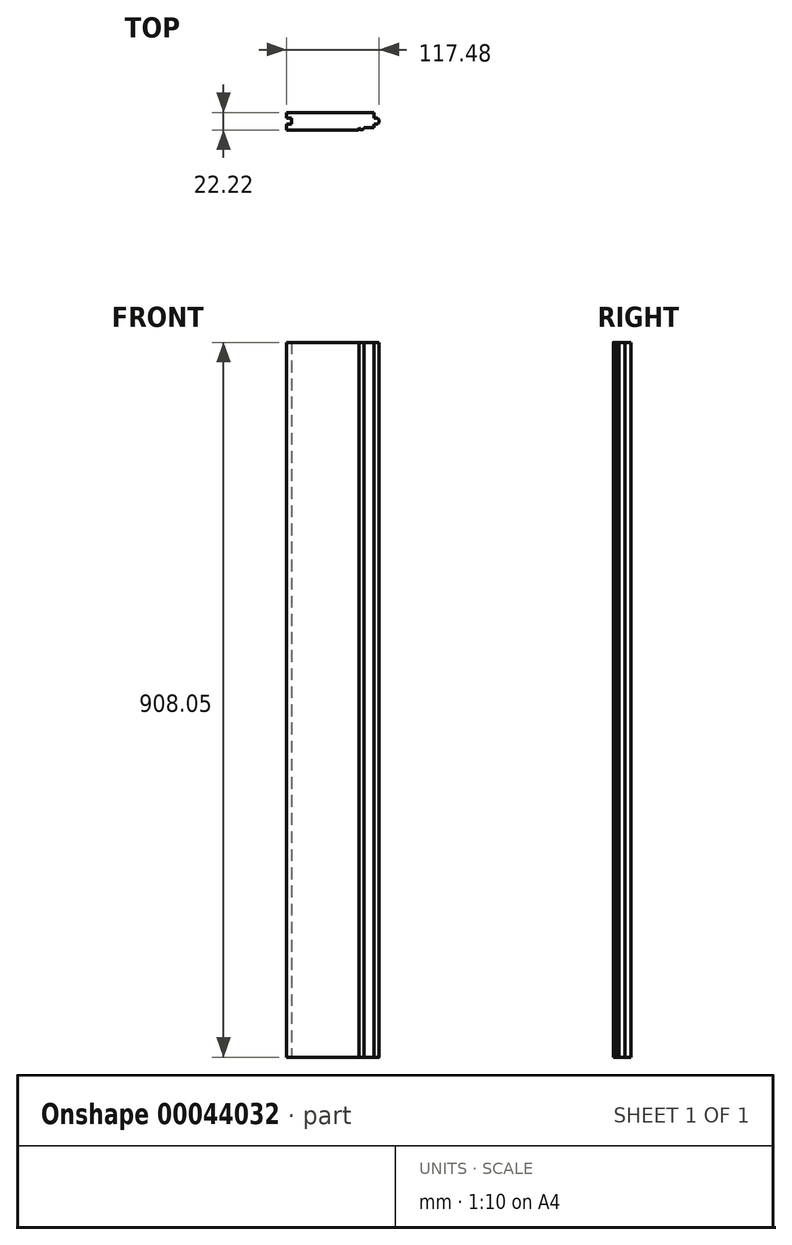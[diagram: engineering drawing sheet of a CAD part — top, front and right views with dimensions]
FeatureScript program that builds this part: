
annotation { "Feature Type Name" : "Feature", "Feature Type Description" : "" }
export const myFeature = defineFeature(function(context is Context, id is Id, definition is map)
    precondition{}
    {
        {
            var Q0;
            Q0=qCreatedBy(makeId("Top.planeOp"),FACE);
            var sketch = newSketch(context, id + "F0", { "sketchPlane" : qUnion([Q0])});
            skLineSegment(sketch, "E0.bottom", {"start": v(58.74, 11.11) * mm, "end": v(-58.74, 11.11) * mm});
            skLineSegment(sketch, "E0.top", {"start": v(58.74, -11.11) * mm, "end": v(-58.74, -11.11) * mm});
            skLineSegment(sketch, "E0.left", {"start": v(58.74, 11.11) * mm, "end": v(58.74, -11.11) * mm});
            skLineSegment(sketch, "E0.right", {"start": v(-58.74, 11.11) * mm, "end": v(-58.74, -11.11) * mm});
            skPoint(sketch, "E0.middle", {"position": v(0, 0) * mm});
            skLineSegment(sketch, "E1", {"start": v(52.39, -11.11) * mm, "end": v(52.39, -3.7) * mm});
            skLineSegment(sketch, "E2", {"start": v(52.39, -3.7) * mm, "end": v(58.74, -3.7) * mm});
            skLineSegment(sketch, "E3", {"start": v(52.39, 11.11) * mm, "end": v(52.39, 3.7) * mm});
            skLineSegment(sketch, "E4", {"start": v(52.39, 3.7) * mm, "end": v(58.74, 3.7) * mm});
            skLineSegment(sketch, "E5", {"start": v(58.74, -3.7) * mm, "end": v(58.74, 3.7) * mm});
            skLineSegment(sketch, "E6", {"start": v(52.39, -7.94) * mm, "end": v(33.34, -7.94) * mm});
            skLineSegment(sketch, "E7", {"start": v(33.34, -7.94) * mm, "end": v(33.34, -11.11) * mm});
            skPoint(sketch, "E8", {"position": v(39.69, -7.94) * mm});
            skPoint(sketch, "E9", {"position": v(46.04, -7.94) * mm});
            skArc(sketch, "E10", {"start": v(33.34, -7.94) * mm, "mid": v(36.51, -11.11) * mm, "end": v(39.69, -7.94) * mm});
            skArc(sketch, "E11.1.0.0", {"start": v(39.69, -7.94) * mm, "mid": v(42.86, -11.11) * mm, "end": v(46.04, -7.94) * mm});
            skArc(sketch, "E11.1.1.0", {"start": v(39.69, -7.94) * mm, "mid": v(42.86, -11.11) * mm, "end": v(46.04, -7.94) * mm});
            skArc(sketch, "E11.2.0.0", {"start": v(46.04, -7.94) * mm, "mid": v(49.21, -11.11) * mm, "end": v(52.39, -7.94) * mm});
            skArc(sketch, "E11.2.1.0", {"start": v(46.04, -7.94) * mm, "mid": v(49.21, -11.11) * mm, "end": v(52.39, -7.94) * mm});
            skLineSegment(sketch, "E11.direction1", {"start": v(33.34, -7.94) * mm, "end": v(39.69, -7.94) * mm, "construction": true});
            skLineSegment(sketch, "E11.direction2", {"start": v(33.34, -7.94) * mm, "end": v(33.34, -7.94) * mm});
            skLineSegment(sketch, "E12", {"start": v(-58.74, -3.7) * mm, "end": v(-52.39, -3.7) * mm});
            skLineSegment(sketch, "E13", {"start": v(-52.39, -3.7) * mm, "end": v(-52.39, 3.7) * mm});
            skLineSegment(sketch, "E14", {"start": v(-52.39, 3.7) * mm, "end": v(-58.74, 3.7) * mm});
            skSolve(sketch);
        }
        {
            var Q0;
            {var subQ0=sQuery(id+"F0.wireOp",EDGE,"E11.2.1.0");var subQ4=makeQuery(id+"F0.imprint","INTERSECT",VERTEX,{"derivedFrom":[sQuery(id+"F0.wireOp",EDGE,"E0.top"),subQ0]});Q0=makeQuery(id+"F0.imprint","IMPRINT",FACE,{"disambiguationData":[TD([[makeQuery(id+"F0.imprint","IMPRINT",EDGE,{"disambiguationData":[TD([[subQ4,1.0]])],"derivedFrom":subQ0}),1.0]])]});}
            var Q1;
            {var subQ0=sQuery(id+"F0.wireOp",EDGE,"E11.1.1.0");var subQ4=makeQuery(id+"F0.imprint","INTERSECT",VERTEX,{"derivedFrom":[sQuery(id+"F0.wireOp",EDGE,"E0.top"),subQ0]});Q1=makeQuery(id+"F0.imprint","IMPRINT",FACE,{"disambiguationData":[TD([[makeQuery(id+"F0.imprint","IMPRINT",EDGE,{"disambiguationData":[TD([[subQ4,1.0]])],"derivedFrom":subQ0}),1.0]])]});}
            var Q2;
            {var subQ0=sQuery(id+"F0.wireOp",EDGE,"E10");var subQ4=makeQuery(id+"F0.imprint","INTERSECT",VERTEX,{"derivedFrom":[sQuery(id+"F0.wireOp",EDGE,"E0.top"),subQ0]});Q2=makeQuery(id+"F0.imprint","IMPRINT",FACE,{"disambiguationData":[TD([[makeQuery(id+"F0.imprint","IMPRINT",EDGE,{"disambiguationData":[TD([[subQ4,1.0]])],"derivedFrom":subQ0}),1.0]])]});}
            var Q3;
            {var subQ7=sQuery(id+"F0.wireOp",EDGE,"E2");Q3=makeQuery(id+"F0.imprint","IMPRINT",FACE,{"disambiguationData":[TD([[makeQuery(id+"F0.imprint","IMPRINT",EDGE,{"derivedFrom":subQ7}),1.0]])]});}
            extrude(context, id + "F1", {"entities" : qUnion([Q0, Q1, Q2, Q3]), "depth" : 908.05 * mm});
        }
        {
            var Q0;
            Q0=makeQuery(id+"F1.opExtrude","SWEPT_EDGE",EDGE,{"disambiguationData":[OSD([sQuery(id+"F0.wireOp",EDGE,"E0.top"),sQuery(id+"F0.wireOp",EDGE,"E7")])]});
            fillet(context, id + "F2", {"entities" : qUnion([Q0]), "radius" : 1.27 * mm, "tangentPropagation" : true, "allowEdgeOverflow" : false});
        }
        {
            var Q0;
            Q0=makeQuery(id+"F1.opExtrude","SWEPT_EDGE",EDGE,{"disambiguationData":[OSD([sQuery(id+"F0.wireOp",EDGE,"E0.left"),sQuery(id+"F0.wireOp",EDGE,"E2"),sQuery(id+"F0.wireOp",EDGE,"E5")])]});
            var Q1;
            Q1=makeQuery(id+"F1.opExtrude","SWEPT_EDGE",EDGE,{"disambiguationData":[OSD([sQuery(id+"F0.wireOp",EDGE,"E0.left"),sQuery(id+"F0.wireOp",EDGE,"E4"),sQuery(id+"F0.wireOp",EDGE,"E5")])]});
            fillet(context, id + "F3", {"entities" : qUnion([Q0, Q1]), "radius" : 3.17 * mm, "tangentPropagation" : true, "allowEdgeOverflow" : false});
        }
    });
